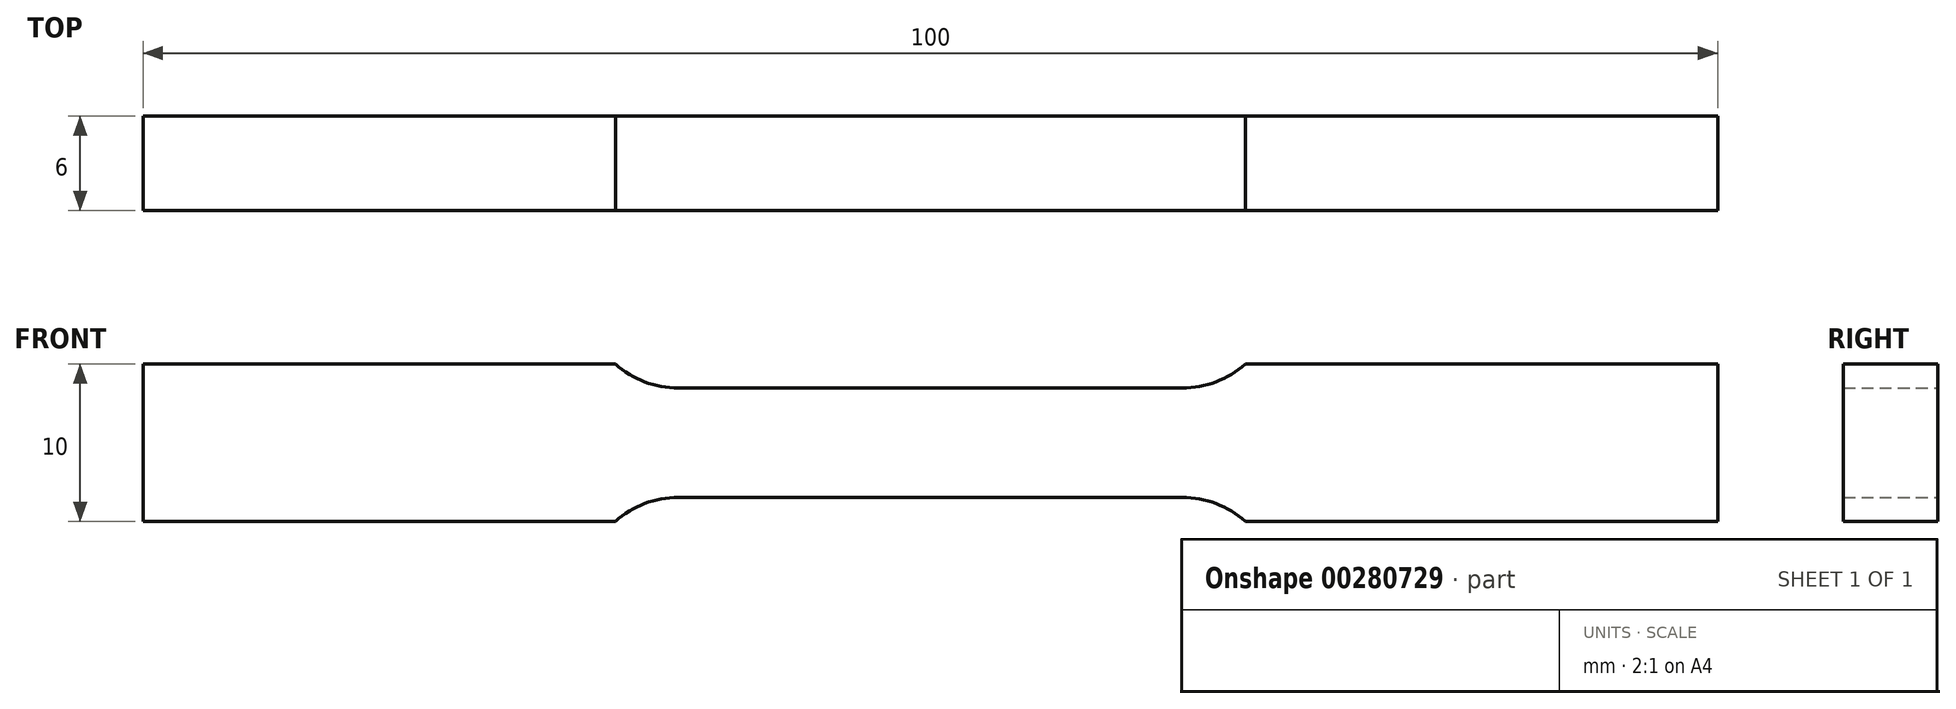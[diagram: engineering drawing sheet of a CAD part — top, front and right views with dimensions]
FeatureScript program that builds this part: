
annotation { "Feature Type Name" : "Feature", "Feature Type Description" : "" }
export const myFeature = defineFeature(function(context is Context, id is Id, definition is map)
    precondition{}
    {
        {
            var Q0;
            Q0=qCreatedBy(makeId("Front.planeOp"),FACE);
            var sketch = newSketch(context, id + "F0", { "sketchPlane" : qUnion([Q0])});
            skLineSegment(sketch, "E0", {"start": v(0, -3.47) * mm, "end": v(16, -3.47) * mm});
            skLineSegment(sketch, "E1", {"start": v(20, 5) * mm, "end": v(50, 5) * mm});
            skLineSegment(sketch, "E2", {"start": v(50, 5) * mm, "end": v(50, 0) * mm});
            skLineSegment(sketch, "E3.MirrorCS", {"start": v(50, -5) * mm, "end": v(50, 0) * mm});
            skLineSegment(sketch, "E4.MirrorCS", {"start": v(20, -5) * mm, "end": v(50, -5) * mm});
            skLineSegment(sketch, "E5.MirrorCS", {"start": v(0, 3.47) * mm, "end": v(16, 3.47) * mm});
            skArc(sketch, "E6", {"start": v(16, 3.47) * mm, "mid": v(18.14, 3.87) * mm, "end": v(20, 5) * mm});
            skArc(sketch, "E7", {"start": v(20, -5) * mm, "mid": v(18.14, -3.87) * mm, "end": v(16, -3.47) * mm});
            skLineSegment(sketch, "E8.MirrorCS", {"start": v(0, 3.47) * mm, "end": v(-16, 3.47) * mm});
            skArc(sketch, "E9.MirrorCS", {"start": v(-16, 3.47) * mm, "mid": v(-18.14, 3.87) * mm, "end": v(-20, 5) * mm});
            skLineSegment(sketch, "E10.MirrorCS", {"start": v(-50, 5) * mm, "end": v(-50, 0) * mm});
            skLineSegment(sketch, "E11.MirrorCS", {"start": v(0, -3.47) * mm, "end": v(-16, -3.47) * mm});
            skArc(sketch, "E12.MirrorCS", {"start": v(-20, -5) * mm, "mid": v(-18.14, -3.87) * mm, "end": v(-16, -3.47) * mm});
            skLineSegment(sketch, "E13.MirrorCS", {"start": v(-50, -5) * mm, "end": v(-50, 0) * mm});
            skLineSegment(sketch, "E14.MirrorCS", {"start": v(-20, -5) * mm, "end": v(-50, -5) * mm});
            skLineSegment(sketch, "E15.MirrorCS", {"start": v(-20, 5) * mm, "end": v(-50, 5) * mm});
            skSolve(sketch);
        }
        {
            var Q0;
            Q0=makeQuery(id+"F0.imprint","IMPRINT",FACE,{"disambiguationData":[TD([[makeQuery(id+"F0.imprint","IMPRINT",EDGE,{"derivedFrom":sQuery(id+"F0.wireOp",EDGE,"E0")}),1.0]])]});
            extrude(context, id + "F1", {"entities" : qUnion([Q0]), "endBound" : BoundingType.SYMMETRIC, "depth" : 6 * mm});
        }
    });
